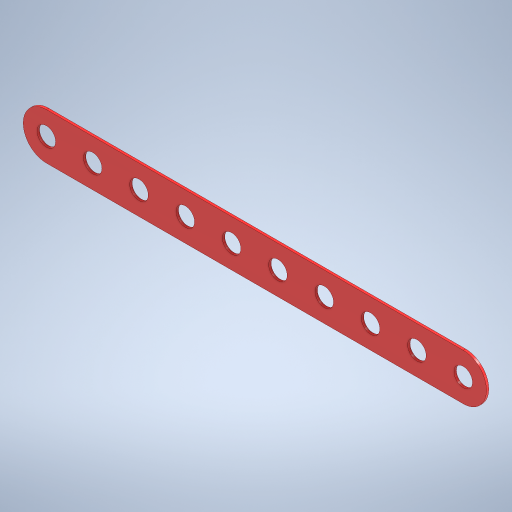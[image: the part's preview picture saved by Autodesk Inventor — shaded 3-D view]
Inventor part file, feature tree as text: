
AUTODESK INVENTOR PART (.ipt)
format: ipt  version: 2024 (Build 280153000, 153)  size: 259,584 bytes
history: native  units: mm
features: extrude x2, sketch x2, other x1, pattern_linear x1
ambient origin geometry x8: Origin, YZ Plane, XZ Plane, XY Plane, X Axis, Y Axis, Z Axis, Center Point
bodies: Body1 (feature_tree)
feature tree (6):
  other  "Těleso1"
  extrude  "Vysunutí1"  Depth=50.0mm
  extrude  "Vysunutí2"  Depth=5.0mm
  pattern_linear  "Obdélníkové pole1"  Spacing1=0.5mm  [1 undecoded]
  sketch  "Náčrt1"
  sketch  "Náčrt2"
note: 1 required parameter value undecoded (feature->parameter linkage not recoverable at this tier; creation-order binding heuristic only, values carry confidence <= 0.55)
